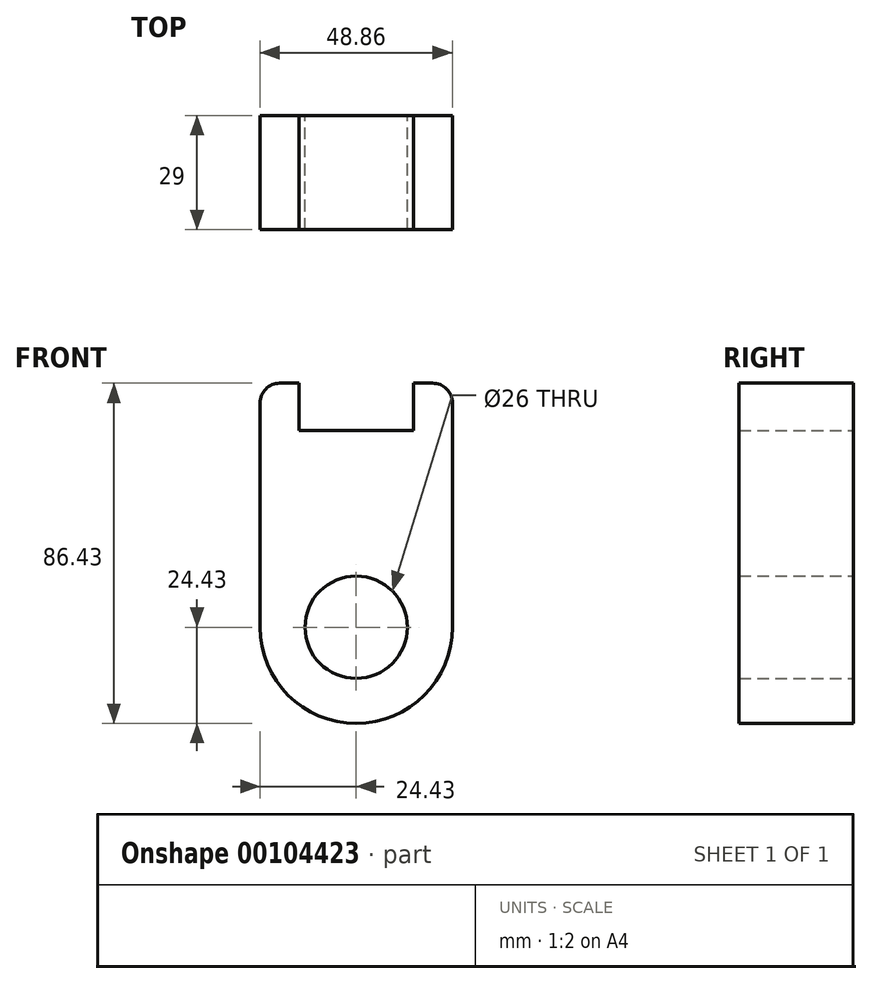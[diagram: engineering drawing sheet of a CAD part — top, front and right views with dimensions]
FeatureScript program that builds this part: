
annotation { "Feature Type Name" : "Feature", "Feature Type Description" : "" }
export const myFeature = defineFeature(function(context is Context, id is Id, definition is map)
    precondition{}
    {
        {
            var Q0;
            Q0=qCreatedBy(makeId("Front.planeOp"),FACE);
            var sketch = newSketch(context, id + "F0", { "sketchPlane" : qUnion([Q0])});
            skCircle(sketch, "E0", {"center": v(0, 0) * mm, "radius": 13 * mm});
            skLineSegment(sketch, "E1.top", {"start": v(-19.43, 62) * mm, "end": v(-14.5, 62) * mm});
            skLineSegment(sketch, "E1.left", {"start": v(-24.43, 0) * mm, "end": v(-24.43, 57) * mm});
            skLineSegment(sketch, "E1.right", {"start": v(24.43, 0) * mm, "end": v(24.43, 57) * mm});
            skArc(sketch, "E2", {"start": v(-24.43, 0) * mm, "mid": v(0, -24.43) * mm, "end": v(24.43, 0) * mm});
            skPoint(sketch, "E3.visualSharp", {"position": v(-24.43, 62) * mm});
            skArc(sketch, "E3.filletArc", {"start": v(-19.43, 62) * mm, "mid": v(-22.97, 60.54) * mm, "end": v(-24.43, 57) * mm});
            skPoint(sketch, "E4.visualSharp", {"position": v(24.43, 62) * mm});
            skArc(sketch, "E4.filletArc", {"start": v(24.43, 57) * mm, "mid": v(22.97, 60.54) * mm, "end": v(19.43, 62) * mm});
            skLineSegment(sketch, "E5", {"start": v(-14.5, 62) * mm, "end": v(-14.5, 50) * mm});
            skLineSegment(sketch, "E6", {"start": v(-14.5, 50) * mm, "end": v(14.5, 50) * mm});
            skLineSegment(sketch, "E7.MirrorCS", {"start": v(14.5, 62) * mm, "end": v(14.5, 50) * mm});
            skLineSegment(sketch, "E8.trimOffspring", {"start": v(14.5, 62) * mm, "end": v(19.43, 62) * mm});
            skSolve(sketch);
        }
        {
            var Q0;
            Q0=makeQuery(id+"F0.imprint","IMPRINT",FACE,{"disambiguationData":[TD([[makeQuery(id+"F0.imprint","IMPRINT",EDGE,{"derivedFrom":sQuery(id+"F0.wireOp",EDGE,"E0")}),-1.0]])]});
            extrude(context, id + "F1", {"entities" : qUnion([Q0]), "depth" : 29 * mm, "offsetDistance" : 25 * mm});
        }
    });
